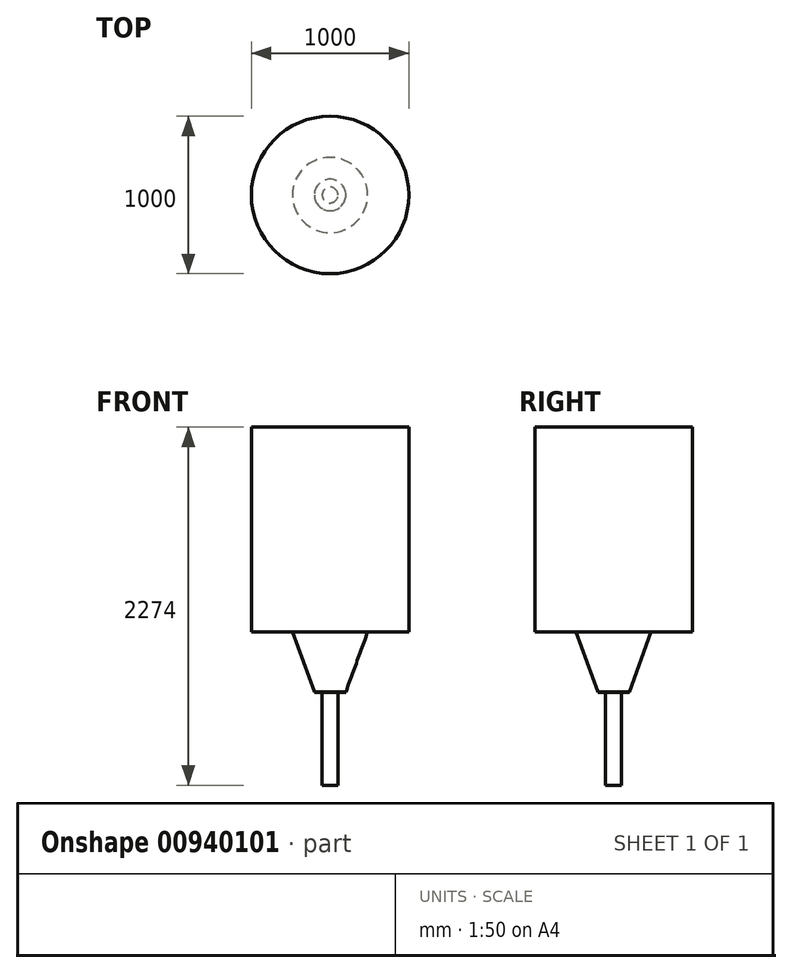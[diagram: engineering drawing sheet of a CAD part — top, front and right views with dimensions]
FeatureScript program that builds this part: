
annotation { "Feature Type Name" : "Feature", "Feature Type Description" : "" }
export const myFeature = defineFeature(function(context is Context, id is Id, definition is map)
    precondition{}
    {
        {
            var Q0;
            Q0=qCreatedBy(makeId("Top.planeOp"),FACE);
            var sketch = newSketch(context, id + "F0", { "sketchPlane" : qUnion([Q0])});
            skCircle(sketch, "E0", {"center": v(0, 0) * mm, "radius": 500 * mm});
            skSolve(sketch);
        }
        {
            var Q0;
            Q0=makeQuery(id+"F0.imprint","IMPRINT",FACE,{"disambiguationData":[TD([[makeQuery(id+"F0.imprint","IMPRINT",EDGE,{"derivedFrom":sQuery(id+"F0.wireOp",EDGE,"E0")}),1.0]])]});
            extrude(context, id + "F1", {"entities" : qUnion([Q0]), "depth" : 1300 * mm, "offsetDistance" : 25 * mm});
        }
        {
            var Q0;
            Q0=makeQuery(id+"F1.opExtrude","CAP_FACE",FACE,{"disambiguationData":[OSD([sQuery(id+"F0.wireOp",EDGE,"E0")])],"isStart":true});
            var sketch = newSketch(context, id + "F2", { "sketchPlane" : qUnion([Q0])});
            skCircle(sketch, "E1", {"center": v(0, 0) * mm, "radius": 150 * mm});
            skSolve(sketch);
        }
        {
            var Q0;
            Q0=qCreatedBy(makeId("Front.planeOp"),FACE);
            var sketch = newSketch(context, id + "F3", { "sketchPlane" : qUnion([Q0])});
            skLineSegment(sketch, "E2", {"start": v(-238.85, 0) * mm, "end": v(0, -656.23) * mm});
            skLineSegment(sketch, "E3", {"start": v(0, 0) * mm, "end": v(0, -656.23) * mm});
            skLineSegment(sketch, "E4.MirrorCS", {"start": v(238.85, 0) * mm, "end": v(0, -656.23) * mm});
            skLineSegment(sketch, "E5", {"start": v(238.85, 0) * mm, "end": v(-238.85, 0) * mm});
            skSolve(sketch);
        }
        {
            var Q0;
            {var subQ0=sQuery(id+"F3.wireOp",EDGE,"E3");Q0=makeQuery(id+"F3.imprint","IMPRINT",FACE,{"disambiguationData":[TD([[makeQuery(id+"F3.imprint","IMPRINT",EDGE,{"derivedFrom":subQ0}),1.0]])]});}
            var Q1;
            Q1=sQuery(id+"F3.wireOp",EDGE,"E3");
            revolve(context, id + "F4", {"operationType" : NewBodyOperationType.ADD, "surfaceOperationType" : NewSurfaceOperationType.NEW, "entities" : qUnion([Q0]), "axis" : qUnion([Q1]), "revolveType" : RevolveType.FULL});
        }
        {
            var Q0;
            Q0=makeQuery(id+"F2.imprint","IMPRINT",FACE,{"disambiguationData":[TD([[makeQuery(id+"F2.imprint","IMPRINT",EDGE,{"derivedFrom":sQuery(id+"F2.wireOp",EDGE,"E1")}),-1.0]])]});
            var sketch = newSketch(context, id + "F5", { "sketchPlane" : qUnion([Q0])});
            skCircle(sketch, "E6", {"center": v(0, 0) * mm, "radius": 100 * mm});
            skSolve(sketch);
        }
        {
            var Q0;
            Q0 = qSketchRegion(id + "F5", true);
            extrude(context, id + "F6", {"entities" : qUnion([Q0]), "operationType" : NewBodyOperationType.REMOVE, "depth" : 809 * mm, "offsetDistance" : 25 * mm});
        }
        {
            var Q0;
            Q0=makeQuery(id+"F2.imprint","IMPRINT",FACE,{"disambiguationData":[TD([[makeQuery(id+"F2.imprint","IMPRINT",EDGE,{"derivedFrom":sQuery(id+"F2.wireOp",EDGE,"E1")}),1.0]])]});
            var sketch = newSketch(context, id + "F7", { "sketchPlane" : qUnion([Q0])});
            skCircle(sketch, "E7", {"center": v(0, 0) * mm, "radius": 100 * mm});
            skSolve(sketch);
        }
        {
            var Q0;
            Q0 = qSketchRegion(id + "F7", true);
            extrude(context, id + "F8", {"entities" : qUnion([Q0]), "operationType" : NewBodyOperationType.ADD, "depth" : 384 * mm, "offsetDistance" : 25 * mm});
        }
        {
            var Q0;
            Q0=makeQuery(id+"F8.opExtrude","CAP_FACE",FACE,{"disambiguationData":[OSD([sQuery(id+"F7.wireOp",EDGE,"E7")])],"isStart":false});
            var sketch = newSketch(context, id + "F9", { "sketchPlane" : qUnion([Q0])});
            skCircle(sketch, "E8", {"center": v(0, 0) * mm, "radius": 50 * mm});
            skSolve(sketch);
        }
        {
            var Q0;
            Q0=makeQuery(id+"F9.imprint","IMPRINT",FACE,{"disambiguationData":[TD([[makeQuery(id+"F9.imprint","IMPRINT",EDGE,{"derivedFrom":sQuery(id+"F9.wireOp",EDGE,"E8")}),1.0]])]});
            var Q1;
            Q1=sQuery(id+"F9.wireOp",EDGE,"E8");
            extrude(context, id + "F10", {"entities" : qUnion([Q0]), "operationType" : NewBodyOperationType.ADD, "surfaceEntities" : qUnion([Q1]), "depth" : 590 * mm, "offsetDistance" : 25 * mm});
        }
    });
